# Revit family: RME-Wall
name_source: partatom
category: Lighting Fixtures
units: mm (PartAtom-declared; Revit-internal decimal feet)

## family parameters
Cut with Voids When Loaded = No
Host = Face
Light Source = Yes
OmniClass Number = 23.80.70.11.21
OmniClass Title = Emergency Lighting
Part Type = Normal
Room Calculation Point = No
Round Connector Dimension = Use Diameter
Shared = No

## types (3) — shared parameters
Color Filter = 16777215
Default Elevation = 48.000"
Description = Running Man Exit Sign
Dimming Lamp Color Temperature Shift = <None>
Emit Shape Visible in Rendering = No
Emit from Rectangle Length = 6.000"
Emit from Rectangle Width = 11.000"
Finish = White
Is 120VAC = Yes
Is 347VAC = No
Lamp = LED Lamp
Lens = Green Glass
Load Classification = Lighting
Manufacturer = Compass Products
Model = RME
Photometric Web File = generic
Tilt Angle = -90.00°
URL = https://www.currentlighting.com
Voltage = 120 V

## per-type parameters (varying)
| type | Apparent Load | Watts |
| RMEUW | 3 VA | 3 W |
| RMEUWE | 2 VA | 2 W |
| RMEUWE-SD | 4 VA | 4 W |

## geometry (parser evidence)
native form markers: Blend x2, Sweep x6
no freeform markers — native parametric forms only
